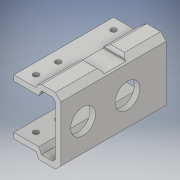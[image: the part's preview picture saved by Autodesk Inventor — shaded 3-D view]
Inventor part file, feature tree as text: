
AUTODESK INVENTOR PART (.ipt)
format: ipt  version: 2018 (Build 220112000, 112)  size: 229,376 bytes
history: native  units: in
note: dims shown in document units (in); Inventor stores cm internally (conversion verified against a paired STEP export)
features: chamfer x6, hole x5, extrude x3, sketch x3
ambient origin geometry x8: Origin, YZ Plane, XZ Plane, XY Plane, X Axis, Y Axis, Z Axis, Center Point
bodies: Body1 (feature_tree)
feature tree (17):
  extrude  "Extrusion2"  Depth=2.0in
  hole  "Hole4"  [1 undecoded]
  hole  "Hole5"  [1 undecoded]
  hole  "Hole6"  [1 undecoded]
  hole  "Hole7"  [1 undecoded]
  hole  "Hole8"  [1 undecoded]
  extrude  "Extrusion3"  Depth=0.25in
  extrude  "Extrusion4"  Depth=1.0in
  chamfer  "Chamfer1"  Distance=0.25in
  chamfer  "Chamfer2"  Distance=0.125in
  chamfer  "Chamfer3"  Distance=0.125in
  chamfer  "Chamfer10"  Distance=0.125in
  chamfer  "Chamfer11"  Distance=0.125in
  chamfer  "Chamfer12"  Distance=0.125in
  sketch  "Sketch1"  dims[d62=1.0in d63=2.0in]
  sketch  "Sketch2"  dims[d64=1.125in d65=0.25in]
  sketch  "Sketch3"  dims[d66=0.25in d67=1.0in d68=0.25in d71=0.125in d72=0.125in d73=0.25in d76=1.0in d77=0.25in d78=0.125in d79=0.125in d80=0.125in d81=0.125in d82=0.125in d83=0.125in d84=4.5in d85=0.0in d86=1.0in d87=1.25in d88=1.125in d89=0.75in d90=0.375in d91=0.25in d92=0.5635in d93=1.0in d94=0.8108in d95=1.25in d96=3.0in d97=1.125in d98=0.75in d99=0.375in d100=0.25in d101=0.5635in d102=1.0in d103=0.8108in d104=0.5in d105=0.5in d106=0.25in d107=0.75in d108=0.375in d109=0.25in d110=0.5635in d111=1.0in d112=0.8108in d113=1.5in d114=0.5in d115=0.25in d116=0.75in d117=0.375in d118=0.25in d119=0.5635in d120=1.0in d121=0.8108in d122=0.5in d123=0.5in d124=0.25in d125=0.75in d126=0.375in d127=0.25in d128=0.5635in d129=1.0in d130=0.8108in d131=0.75in d132=3.0in d133=0.25in d134=0.25in d135=0.0in d136=2.0in d138=3.0in d139=0.0in d140=0.125in d141=0.125in d142=45.0deg d143=0.125in d144=0.125in d145=45.0deg d146=0.125in d147=0.125in d148=45.0deg d167=0.125in d168=0.125in d169=45.0deg d170=0.1875in d171=0.125in d172=0.125in d173=45.0deg d174=0.125in d175=0.125in d176=45.0deg]
note: 5 required parameter values undecoded (feature->parameter linkage not recoverable at this tier; creation-order binding heuristic only, values carry confidence <= 0.55)
